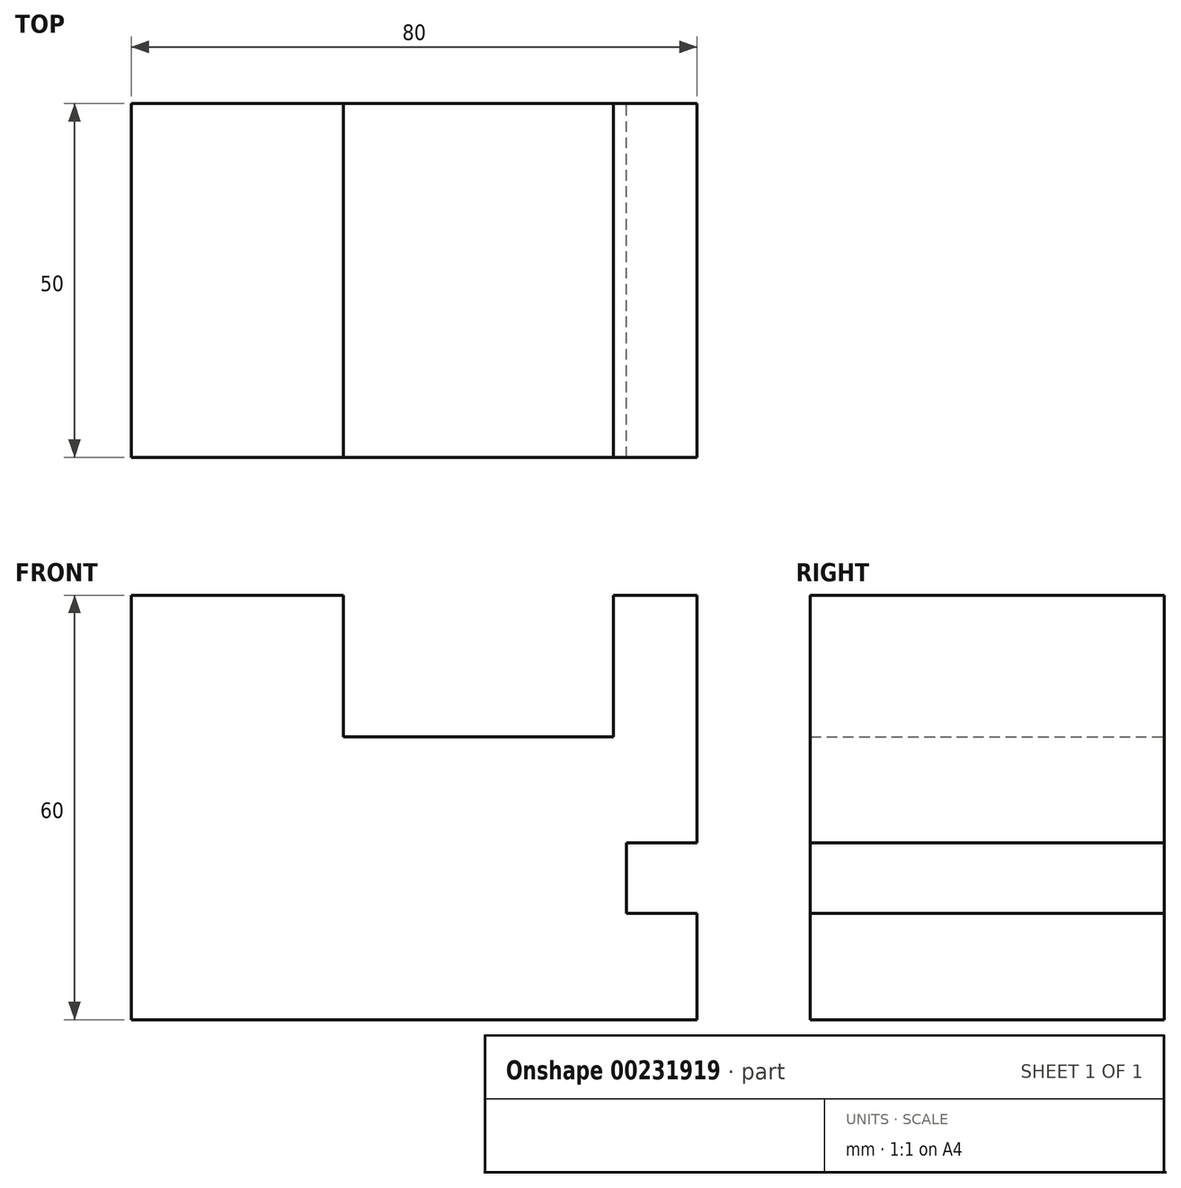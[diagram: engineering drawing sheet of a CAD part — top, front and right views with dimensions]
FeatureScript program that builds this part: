
annotation { "Feature Type Name" : "Feature", "Feature Type Description" : "" }
export const myFeature = defineFeature(function(context is Context, id is Id, definition is map)
    precondition{}
    {
        {
            var Q0;
            Q0=qCreatedBy(makeId("Front.planeOp"),FACE);
            var sketch = newSketch(context, id + "F0", { "sketchPlane" : qUnion([Q0])});
            skLineSegment(sketch, "E0", {"start": v(-80, 60) * mm, "end": v(-50, 60) * mm});
            skLineSegment(sketch, "E1", {"start": v(-50, 60) * mm, "end": v(-50, 40) * mm});
            skLineSegment(sketch, "E2", {"start": v(-50, 40) * mm, "end": v(-11.86, 40) * mm});
            skLineSegment(sketch, "E3", {"start": v(-11.86, 40) * mm, "end": v(-11.86, 60) * mm});
            skLineSegment(sketch, "E4", {"start": v(-11.86, 60) * mm, "end": v(0, 60) * mm});
            skLineSegment(sketch, "E5", {"start": v(0, 60) * mm, "end": v(0, 25) * mm});
            skLineSegment(sketch, "E6", {"start": v(0, 25) * mm, "end": v(-10, 25) * mm});
            skLineSegment(sketch, "E7", {"start": v(-10, 25) * mm, "end": v(-10, 15) * mm});
            skLineSegment(sketch, "E8", {"start": v(-10, 15) * mm, "end": v(0, 15) * mm});
            skLineSegment(sketch, "E9", {"start": v(0, 15) * mm, "end": v(0, 0) * mm});
            skLineSegment(sketch, "E10", {"start": v(0, 0) * mm, "end": v(-80, 0) * mm});
            skLineSegment(sketch, "E11", {"start": v(-80, 60) * mm, "end": v(-80, 0) * mm});
            skSolve(sketch);
        }
        {
            var Q0;
            Q0=makeQuery(id+"F0.imprint","IMPRINT",FACE,{"disambiguationData":[TD([[makeQuery(id+"F0.imprint","IMPRINT",EDGE,{"derivedFrom":sQuery(id+"F0.wireOp",EDGE,"E0")}),-1.0]])]});
            extrude(context, id + "F1", {"entities" : qUnion([Q0]), "depth" : 25 * mm});
        }
        {
            var Q0;
            Q0=makeQuery(id+"F1.opExtrude","CAP_FACE",FACE,{"disambiguationData":[OSD([sQuery(id+"F0.wireOp",EDGE,"E0"),sQuery(id+"F0.wireOp",EDGE,"E1"),sQuery(id+"F0.wireOp",EDGE,"E2"),sQuery(id+"F0.wireOp",EDGE,"E3"),sQuery(id+"F0.wireOp",EDGE,"E4"),sQuery(id+"F0.wireOp",EDGE,"E5"),sQuery(id+"F0.wireOp",EDGE,"E6"),sQuery(id+"F0.wireOp",EDGE,"E7"),sQuery(id+"F0.wireOp",EDGE,"E8"),sQuery(id+"F0.wireOp",EDGE,"E9"),sQuery(id+"F0.wireOp",EDGE,"E10"),sQuery(id+"F0.wireOp",EDGE,"E11")])],"isStart":false});
            extrude(context, id + "F2", {"entities" : qUnion([Q0]), "operationType" : NewBodyOperationType.ADD, "depth" : 25 * mm});
        }
    });
